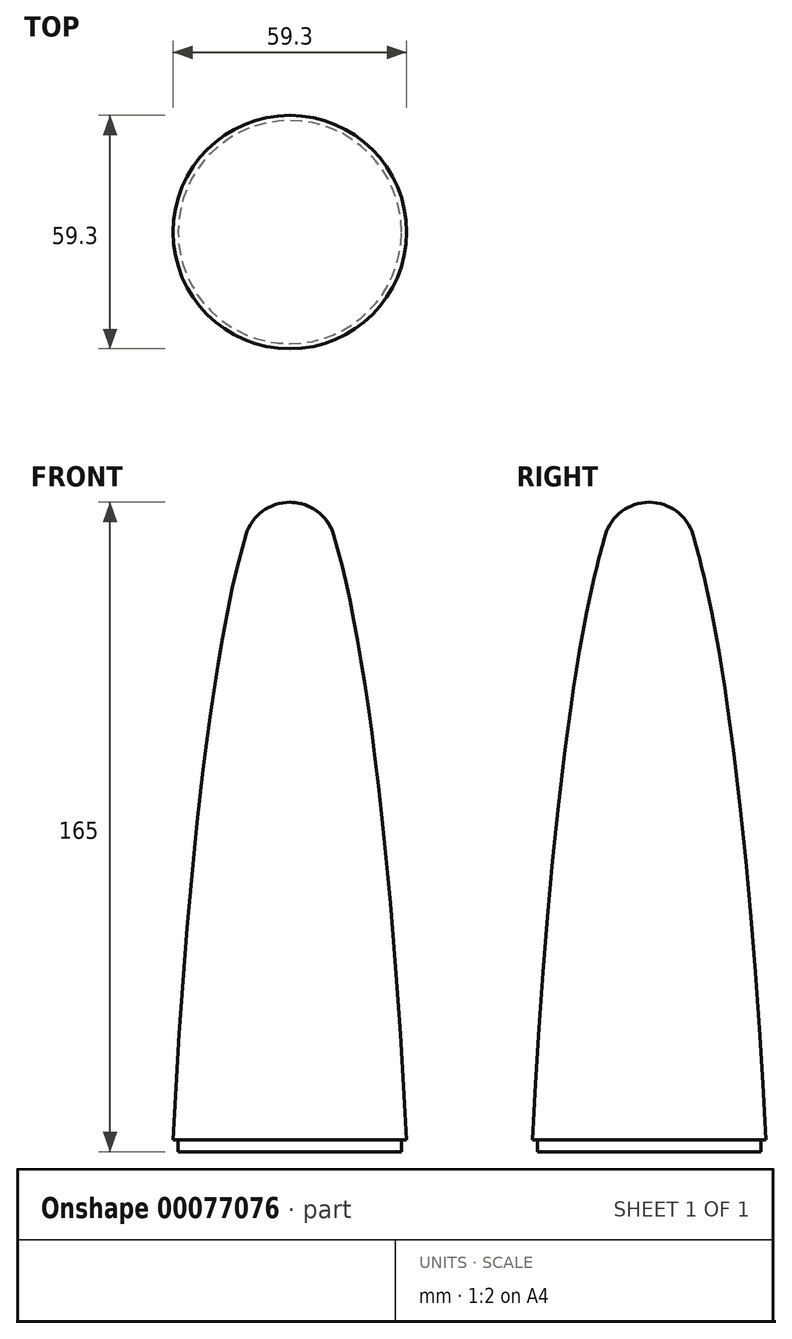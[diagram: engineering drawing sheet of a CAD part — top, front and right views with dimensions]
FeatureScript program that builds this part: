
annotation { "Feature Type Name" : "Feature", "Feature Type Description" : "" }
export const myFeature = defineFeature(function(context is Context, id is Id, definition is map)
    precondition{}
    {
        {
            var Q0;
            Q0=qCreatedBy(makeId("Front.planeOp"),FACE);
            var sketch = newSketch(context, id + "F0", { "sketchPlane" : qUnion([Q0])});
            skLineSegment(sketch, "E0", {"start": v(0, 294) * mm, "end": v(0, 288.28) * mm, "construction": true});
            skPoint(sketch, "E0.endSnap0", {"position": v(0, 294) * mm});
            skLineSegment(sketch, "E1.top", {"start": v(-28.36, 123.06) * mm, "end": v(-29.65, 123.06) * mm});
            skLineSegment(sketch, "E1.left", {"start": v(0, 288.28) * mm, "end": v(0, 123.06) * mm});
            skPoint(sketch, "E1.right.start.orphan", {"position": v(-63.28, 294) * mm});
            skPoint(sketch, "E2.orphan", {"position": v(-63.28, 123.06) * mm});
            skLineSegment(sketch, "E3.trimOffspring", {"start": v(0, 123.06) * mm, "end": v(0, 288.28) * mm});
            skPoint(sketch, "E4.orphan", {"position": v(0, 67.2) * mm});
            skLineSegment(sketch, "E5.top", {"start": v(0, 120.06) * mm, "end": v(-28.36, 120.06) * mm});
            skLineSegment(sketch, "E5.left", {"start": v(0, 123.06) * mm, "end": v(0, 120.06) * mm});
            skLineSegment(sketch, "E5.right", {"start": v(-28.36, 123.06) * mm, "end": v(-28.36, 120.06) * mm});
            skPoint(sketch, "E6.center.orphan", {"position": v(0, 0) * mm});
            skLineSegment(sketch, "E7", {"start": v(-9.02, 283.05) * mm, "end": v(-9.02, 283.05) * mm});
            skEllipticalArc(sketch, "E8", {});
            skLineSegment(sketch, "E9.trimOffspring", {"start": v(0, 291) * mm, "end": v(0, -294) * mm, "construction": true});
            skLineSegment(sketch, "E10", {"start": v(0, 291) * mm, "end": v(0, 120.06) * mm});
            skArc(sketch, "E11", {"start": v(0, 285.06) * mm, "mid": v(-6.93, 282.77) * mm, "end": v(-11.12, 276.8) * mm});
            skLineSegment(sketch, "E12.trimOffspring", {"start": v(0, 285.06) * mm, "end": v(0, 123.06) * mm, "construction": true});
            const initialGuessF0  = {"E8": [0.00037996361933036085, 0.0012328408560738225, 0, 1, 0.294, 0.033, 0.35603298912241194, 1.1435512876573168]};
            skSetInitialGuess(sketch, initialGuessF0);
            skSolve(sketch);
        }
        {
            var Q0;
            Q0=makeQuery(id+"F0.imprint","IMPRINT",FACE,{"disambiguationData":[TD([[makeQuery(id+"F0.imprint","IMPRINT",EDGE,{"derivedFrom":sQuery(id+"F0.wireOp",EDGE,"E1.top")}),-1.0]])]});
            var Q1;
            Q1=sQuery(id+"F0.wireOp",EDGE,"E0");
            revolve(context, id + "F1", {"entities" : qUnion([Q0]), "axis" : qUnion([Q1]), "revolveType" : RevolveType.FULL});
        }
        {
            var Q0;
            Q0=makeQuery(id+"F1.opRevolve","SWEPT_BODY",BODY,{"disambiguationData":[OSD([sQuery(id+"F0.wireOp",EDGE,"E1.top"),sQuery(id+"F0.wireOp",EDGE,"E3.trimOffspring"),sQuery(id+"F0.wireOp",EDGE,"E5.top"),sQuery(id+"F0.wireOp",EDGE,"E5.left"),sQuery(id+"F0.wireOp",EDGE,"E5.right"),sQuery(id+"F0.wireOp",EDGE,"988e126a-8830-41c9-8f9b-90423b33b9f4"),sQuery(id+"F0.wireOp",EDGE,"6f054b1e-dafb-45bf-af7e-3cf8252b6038")])]});
            transform(context, id + "F2", {"entities" : qUnion([Q0]), "transformType" : TransformType.TRANSLATION_3D, "dx" : 0 * mm, "dy" : 0 * mm, "dz" : -220 * mm, "makeCopy" : false});
        }
    });
